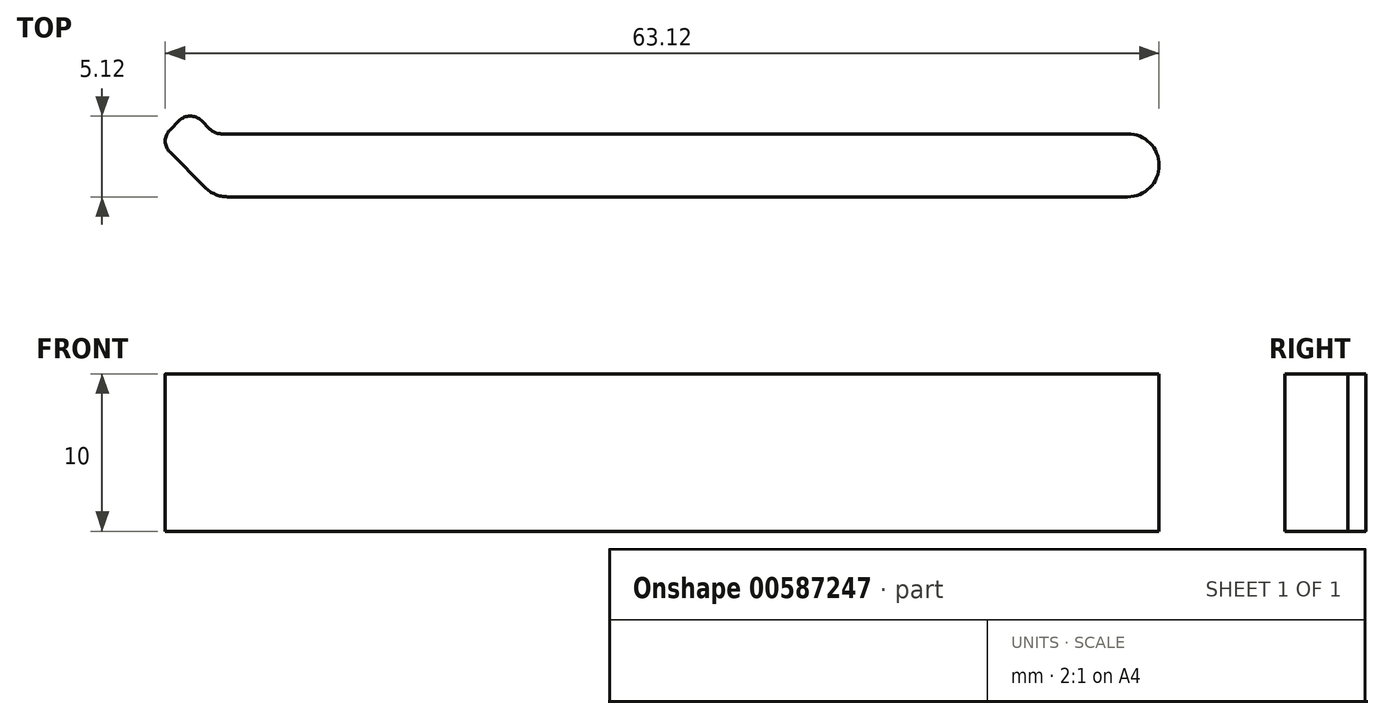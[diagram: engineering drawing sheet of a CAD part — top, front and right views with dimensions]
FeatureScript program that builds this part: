
annotation { "Feature Type Name" : "Feature", "Feature Type Description" : "" }
export const myFeature = defineFeature(function(context is Context, id is Id, definition is map)
    precondition{}
    {
        {
            var Q0;
            Q0=qCreatedBy(makeId("Top.planeOp"),FACE);
            var sketch = newSketch(context, id + "F0", { "sketchPlane" : qUnion([Q0])});
            skLineSegment(sketch, "E0.bottom", {"start": v(0.83, 0) * mm, "end": v(58, 0) * mm});
            skLineSegment(sketch, "E0.top", {"start": v(0.41, 4) * mm, "end": v(58, 4) * mm});
            skLineSegment(sketch, "E0.left", {"start": v(0, 0) * mm, "end": v(0, 0.18) * mm});
            skLineSegment(sketch, "E0.right", {"start": v(60, 2) * mm, "end": v(60, 2) * mm});
            skPoint(sketch, "E1.center.orphan", {"position": v(0, 2) * mm});
            skLineSegment(sketch, "E2", {"start": v(-0.59, 0.59) * mm, "end": v(-2.83, 2.83) * mm});
            skLineSegment(sketch, "E3", {"start": v(-2.83, 4.24) * mm, "end": v(-2.24, 4.83) * mm});
            skLineSegment(sketch, "E4", {"start": v(-0.83, 4.83) * mm, "end": v(-0.3, 4.3) * mm});
            skPoint(sketch, "E5.visualSharp", {"position": v(0, 0) * mm});
            skArc(sketch, "E5.filletArc", {"start": v(-0.59, 0.59) * mm, "mid": v(0.06, 0.15) * mm, "end": v(0.83, 0) * mm});
            skPoint(sketch, "E6.visualSharp", {"position": v(-3.54, 3.54) * mm});
            skArc(sketch, "E6.filletArc", {"start": v(-2.83, 4.24) * mm, "mid": v(-3.12, 3.54) * mm, "end": v(-2.83, 2.83) * mm});
            skPoint(sketch, "E7.visualSharp", {"position": v(-1.54, 5.54) * mm});
            skArc(sketch, "E7.filletArc", {"start": v(-0.83, 4.83) * mm, "mid": v(-1.54, 5.12) * mm, "end": v(-2.24, 4.83) * mm});
            skPoint(sketch, "E8.visualSharp", {"position": v(0, 4) * mm});
            skArc(sketch, "E8.filletArc", {"start": v(-0.3, 4.3) * mm, "mid": v(0.03, 4.08) * mm, "end": v(0.41, 4) * mm});
            skPoint(sketch, "E9.visualSharp", {"position": v(60, 4) * mm});
            skArc(sketch, "E9.filletArc", {"start": v(60, 2) * mm, "mid": v(59.41, 3.41) * mm, "end": v(58, 4) * mm});
            skPoint(sketch, "E10.visualSharp", {"position": v(60, 0) * mm});
            skArc(sketch, "E10.filletArc", {"start": v(58, 0) * mm, "mid": v(59.41, 0.59) * mm, "end": v(60, 2) * mm});
            skSolve(sketch);
        }
        {
            var Q0;
            {var subQ1=sQuery(id+"F0.wireOp",EDGE,"E0.bottom");Q0=makeQuery(id+"F0.imprint","IMPRINT",FACE,{"disambiguationData":[TD([[makeQuery(id+"F0.imprint","IMPRINT",EDGE,{"derivedFrom":subQ1}),1.0]])]});}
            extrude(context, id + "F1", {"entities" : qUnion([Q0]), "depth" : 10 * mm, "offsetDistance" : 25 * mm});
        }
    });
